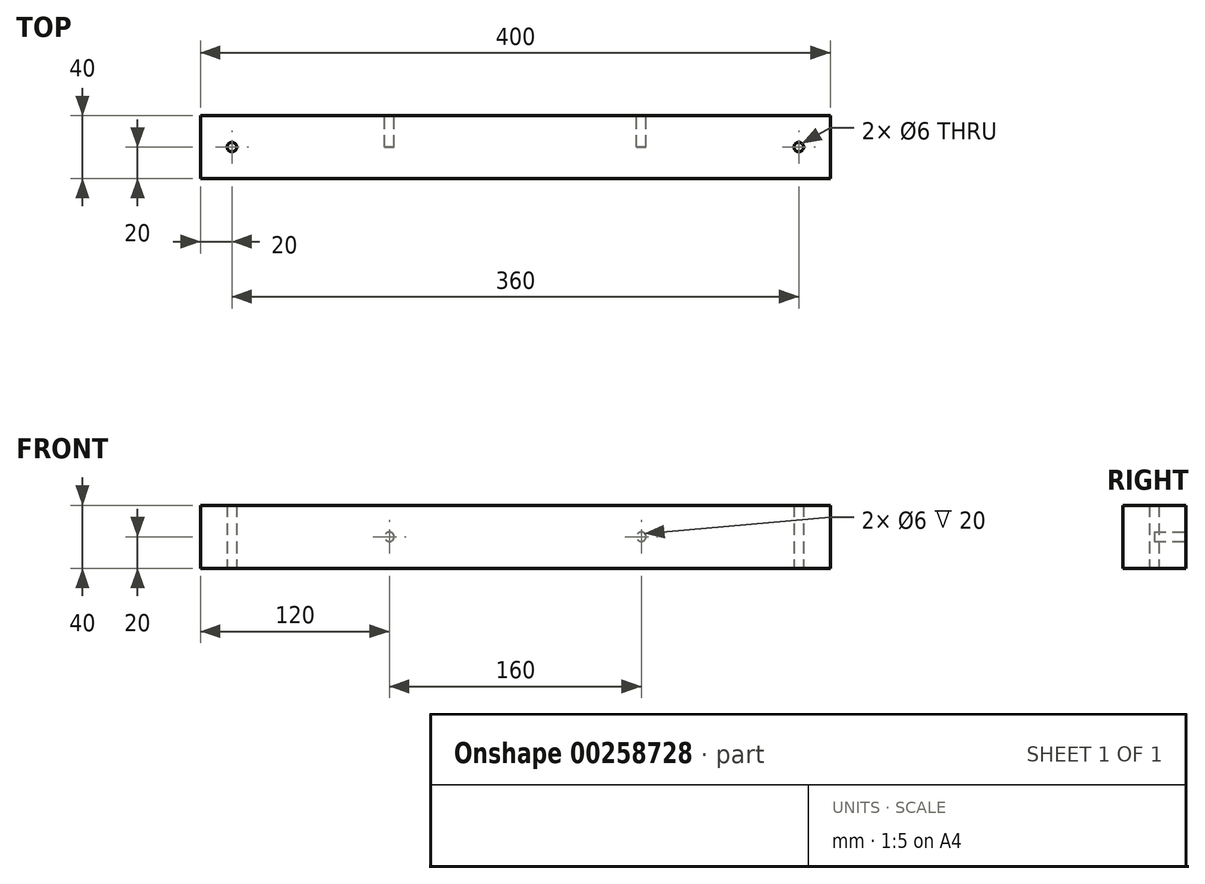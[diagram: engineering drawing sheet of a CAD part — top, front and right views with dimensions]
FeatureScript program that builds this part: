
annotation { "Feature Type Name" : "Feature", "Feature Type Description" : "" }
export const myFeature = defineFeature(function(context is Context, id is Id, definition is map)
    precondition{}
    {
        {
            var Q0;
            Q0=qCreatedBy(makeId("Top.planeOp"),FACE);
            var sketch = newSketch(context, id + "F0", { "sketchPlane" : qUnion([Q0])});
            skLineSegment(sketch, "E0.bottom", {"start": v(0, 0) * mm, "end": v(400, 0) * mm});
            skLineSegment(sketch, "E0.top", {"start": v(0, 40) * mm, "end": v(400, 40) * mm});
            skLineSegment(sketch, "E0.left", {"start": v(0, 0) * mm, "end": v(0, 40) * mm});
            skLineSegment(sketch, "E0.right", {"start": v(400, 0) * mm, "end": v(400, 40) * mm});
            skCircle(sketch, "E1", {"center": v(20, 20) * mm, "radius": 3 * mm});
            skCircle(sketch, "E2", {"center": v(380, 20) * mm, "radius": 3 * mm});
            skPoint(sketch, "E2.centerSnap0", {"position": v(400, 20) * mm});
            skSolve(sketch);
        }
        {
            var Q0;
            Q0=makeQuery(id+"F0.imprint","IMPRINT",FACE,{"disambiguationData":[TD([[makeQuery(id+"F0.imprint","IMPRINT",EDGE,{"derivedFrom":sQuery(id+"F0.wireOp",EDGE,"E0.bottom")}),1.0]])]});
            extrude(context, id + "F1", {"entities" : qUnion([Q0]), "depth" : 40 * mm});
        }
        {
            var Q0;
            Q0=makeQuery(id+"F1.opExtrude","SWEPT_FACE",FACE,{"disambiguationData":[OSD([sQuery(id+"F0.wireOp",EDGE,"E0.top")])]});
            var sketch = newSketch(context, id + "F2", { "sketchPlane" : qUnion([Q0])});
            skLineSegment(sketch, "E3.0", {"start": v(0, 40) * mm, "end": v(-400, 40) * mm});
            skLineSegment(sketch, "E4.0", {"start": v(0, 0) * mm, "end": v(-400, 0) * mm});
            skLineSegment(sketch, "E5.0", {"start": v(0, 40) * mm, "end": v(0, 0) * mm});
            skLineSegment(sketch, "E6.0", {"start": v(-400, 40) * mm, "end": v(-400, 0) * mm});
            skCircle(sketch, "E7", {"center": v(-120, 20) * mm, "radius": 3 * mm});
            skPoint(sketch, "E7.centerSnap0", {"position": v(0, 20) * mm});
            skCircle(sketch, "E8", {"center": v(-280, 20) * mm, "radius": 3 * mm});
            skPoint(sketch, "E8.centerSnap0", {"position": v(-400, 20) * mm});
            skSolve(sketch);
        }
        {
            var Q0;
            Q0=makeQuery(id+"F2.imprint","IMPRINT",FACE,{"disambiguationData":[TD([[makeQuery(id+"F2.imprint","IMPRINT",EDGE,{"derivedFrom":sQuery(id+"F2.wireOp",EDGE,"E7")}),1.0]])]});
            var Q1;
            Q1=sQuery(id+"F2.wireOp",EDGE,"E7");
            extrude(context, id + "F4", {"entities" : qUnion([Q0]), "operationType" : NewBodyOperationType.REMOVE, "surfaceEntities" : qUnion([Q1]), "oppositeDirection" : true, "depth" : 20 * mm});
        }
        {
            var Q0;
            Q0=makeQuery(id+"F1.opExtrude","SWEPT_FACE",FACE,{"disambiguationData":[OSD([sQuery(id+"F0.wireOp",EDGE,"E0.top")])]});
            var sketch = newSketch(context, id + "F3", { "sketchPlane" : qUnion([Q0])});
            skCircle(sketch, "E9", {"center": v(-280, 20) * mm, "radius": 3 * mm});
            skPoint(sketch, "E9.centerSnap0", {"position": v(-400, 20) * mm});
            skSolve(sketch);
        }
        {
            var Q0;
            Q0=makeQuery(id+"F3.imprint","IMPRINT",FACE,{"disambiguationData":[TD([[makeQuery(id+"F3.imprint","IMPRINT",EDGE,{"derivedFrom":sQuery(id+"F3.wireOp",EDGE,"E9")}),1.0]])]});
            var Q1;
            Q1=sQuery(id+"F3.wireOp",EDGE,"E9");
            extrude(context, id + "F5", {"entities" : qUnion([Q0]), "operationType" : NewBodyOperationType.REMOVE, "surfaceEntities" : qUnion([Q1]), "oppositeDirection" : true, "depth" : 20 * mm});
        }
    });
